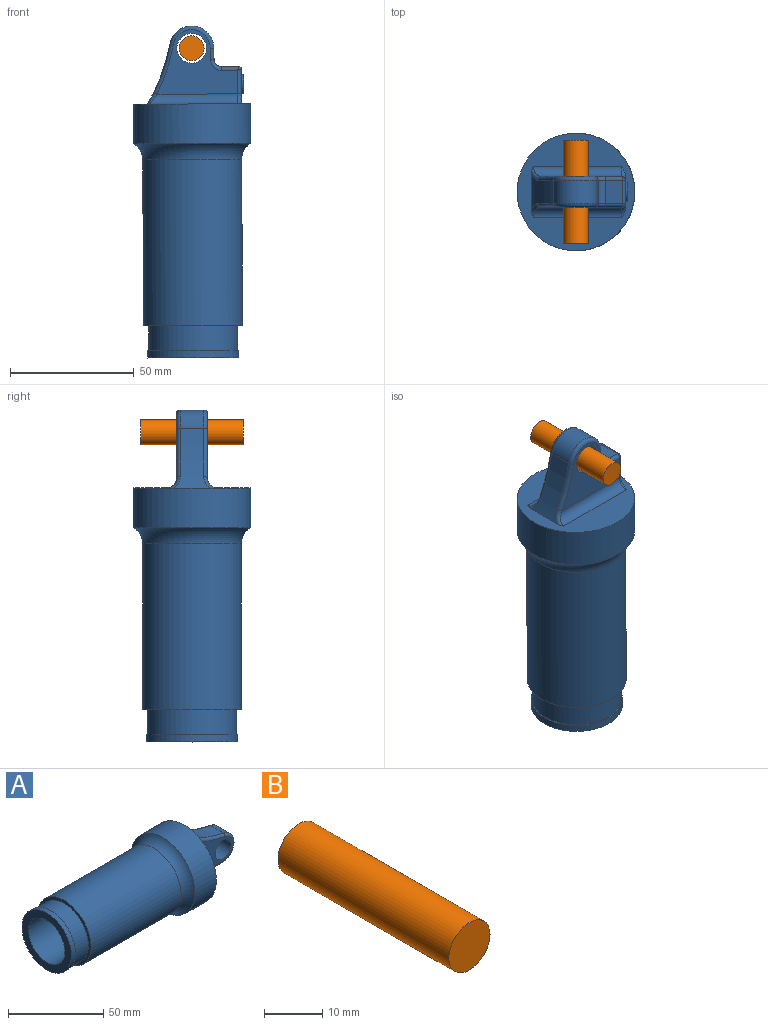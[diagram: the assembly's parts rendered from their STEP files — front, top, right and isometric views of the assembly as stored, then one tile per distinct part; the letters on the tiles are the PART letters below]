
ASSEMBLY  parts=2 mates=1
PART A: 43 faces, bbox 135.2x60x60 mm
  f0: plane 9.5x4.5mm, normal (0,0,-1), area 42.8mm2, adj f12,f22,f27,f36
  f1: plane 47.93x47.93mm, normal (1,0,0), area 998.8mm2, adj f5,f13,f17,f18,f19,f24,f32,f33
  f2: plane 36.8x36.8mm, normal (-1,0,0), area 491.1mm2, adj f3,f11
  f3: cylinder r=13.5mm len=86.5mm, axis (-1,0,0), area 7337.2mm2, adj f2,f4
  f4: plane 27x27mm, normal (-1,0,0), area 572.6mm2, adj f3
  f5: cylinder r=23.75mm len=47.5mm, axis (-1,0,0), area 2387.6mm2, adj f1,f6
  f6: torus R=27.51mm, axis (-1,0,0), area 1051.5mm2, adj f5,f7
  f7: cylinder r=20mm len=67mm, axis (-1,0,0), area 8419.5mm2, adj f6,f8
  f8: plane 40x40mm, normal (-1,0,0), area 238.8mm2, adj f7,f9
  f9: cylinder r=18mm len=36mm, axis (-1,0,0), area 1131mm2, adj f8,f10
  f10: plane 36.8x36.8mm, normal (1,0,0), area 45.7mm2, adj f9,f11
  f11: cylinder r=18.4mm len=36.8mm, axis (-1,0,0), area 346.8mm2, adj f2,f10
  f12: cylinder r=9mm len=17.84mm, axis (0,1,0), area 252.5mm2, adj f0,f13,f26,f35
  f13: cylinder r=75mm len=24.19mm, axis (0,1,0), area 261.6mm2, adj f1,f12,f24,f25,f33,f34
  f14: plane 32.61x26mm, normal (0,-1,0), area 415.9mm2, adj f19,f25,f26,f27,f28,f29,f31,f42
  f15: plane 32.61x26mm, normal (0,1,0), area 415.9mm2, adj f18,f34,f35,f36,f37,f38,f40,f42
  f16: plane 9.5x7mm, normal (1,0,0), area 66.5mm2, adj f22,f23,f29,f38
  f17: plane 14x12.95mm, normal (0,0,-1), area 87mm2, adj f1,f20,f23,f31,f32,f40,f41
  f18: cylinder r=4mm len=35.65mm, axis (0,0,-1), area 214.4mm2, adj f1,f15,f33,f41
  f19: cylinder r=4mm len=35.65mm, axis (0,0,1), area 214.4mm2, adj f1,f14,f24,f32
  f20: cylinder r=4mm len=8mm, axis (0,0,1), area 25.1mm2, adj f17,f21
  f21: plane 8x8mm, normal (0,0,-1), area 50.3mm2, adj f20
  f22: cylinder r=3mm len=9.5mm, axis (0,-1,0), area 44.8mm2, adj f0,f16,f28,f37
  f23: cylinder r=1mm len=9.5mm, axis (0,1,0), area 14.9mm2, adj f16,f17,f30,f39
  f24: bspline ~6.69x6.15mm, area 12.8mm2, adj f1,f13,f19,f25
  f25: torus R=76.5mm, axis (0,-1,0), area 49.1mm2, adj f13,f14,f24,f26
  f26: torus R=7.5mm, axis (0,-1,0), area 58.8mm2, adj f12,f14,f25,f27
  f27: cylinder r=1.5mm len=4.5mm, axis (-1,0,0), area 10.6mm2, adj f0,f14,f26,f28
  f28: torus R=4.5mm, axis (0,-1,0), area 13.1mm2, adj f14,f22,f27,f29
  f29: cylinder r=1.5mm len=7mm, axis (0,0,1), area 15.9mm2, adj f14,f16,f28,f30
  f30: bspline ~1.58x1.5mm, area 1.6mm2, adj f23,f29,f31
  f31: cylinder r=1.5mm len=10mm, axis (-1,0,0), area 23mm2, adj f14,f17,f30,f32
  f32: torus R=5.5mm, axis (0,0,-1), area 12.5mm2, adj f1,f17,f19,f31
  f33: bspline ~6.69x6.15mm, area 12.8mm2, adj f1,f13,f18,f34
  f34: torus R=76.5mm, axis (0,-1,0), area 49.1mm2, adj f13,f15,f33,f35
  f35: torus R=7.5mm, axis (0,-1,0), area 58.8mm2, adj f12,f15,f34,f36
  f36: cylinder r=1.5mm len=4.5mm, axis (1,0,0), area 10.6mm2, adj f0,f15,f35,f37
  f37: torus R=4.5mm, axis (0,-1,0), area 13.1mm2, adj f15,f22,f36,f38
  f38: cylinder r=1.5mm len=7mm, axis (0,0,-1), area 15.9mm2, adj f15,f16,f37,f39
  f39: bspline ~1.58x1.5mm, area 1.6mm2, adj f23,f38,f40
  f40: cylinder r=1.5mm len=10mm, axis (1,0,0), area 23mm2, adj f15,f17,f39,f41
  f41: torus R=5.5mm, axis (0,0,-1), area 12.5mm2, adj f1,f17,f18,f40
  f42: cylinder r=6mm len=12.5mm, axis (0,-1,0), area 471.2mm2, adj f14,f15
PART B: 3 faces, bbox 10x41.5x10 mm
  f0: cylinder r=5mm len=41.5mm, axis (0,-1,0), area 1303.9mm2, adj f1,f2
  f1: plane 10x10mm, normal (0,1,0), area 78.5mm2, adj f0
  f2: plane 10x10mm, normal (0,-1,0), area 78.5mm2, adj f0
PLACE A rot(axis=(0,-1,0),90.3deg) t=(3.33,-20.35,51.25)mm
PLACE B rot(axis=(0,-1,0),90.3deg) t=(2.29,-20.35,251.24)mm
MATE fastened B.f0 <-> A.f42  axis (0,-1,0) through (2.29,-20.35,251.24)mm
